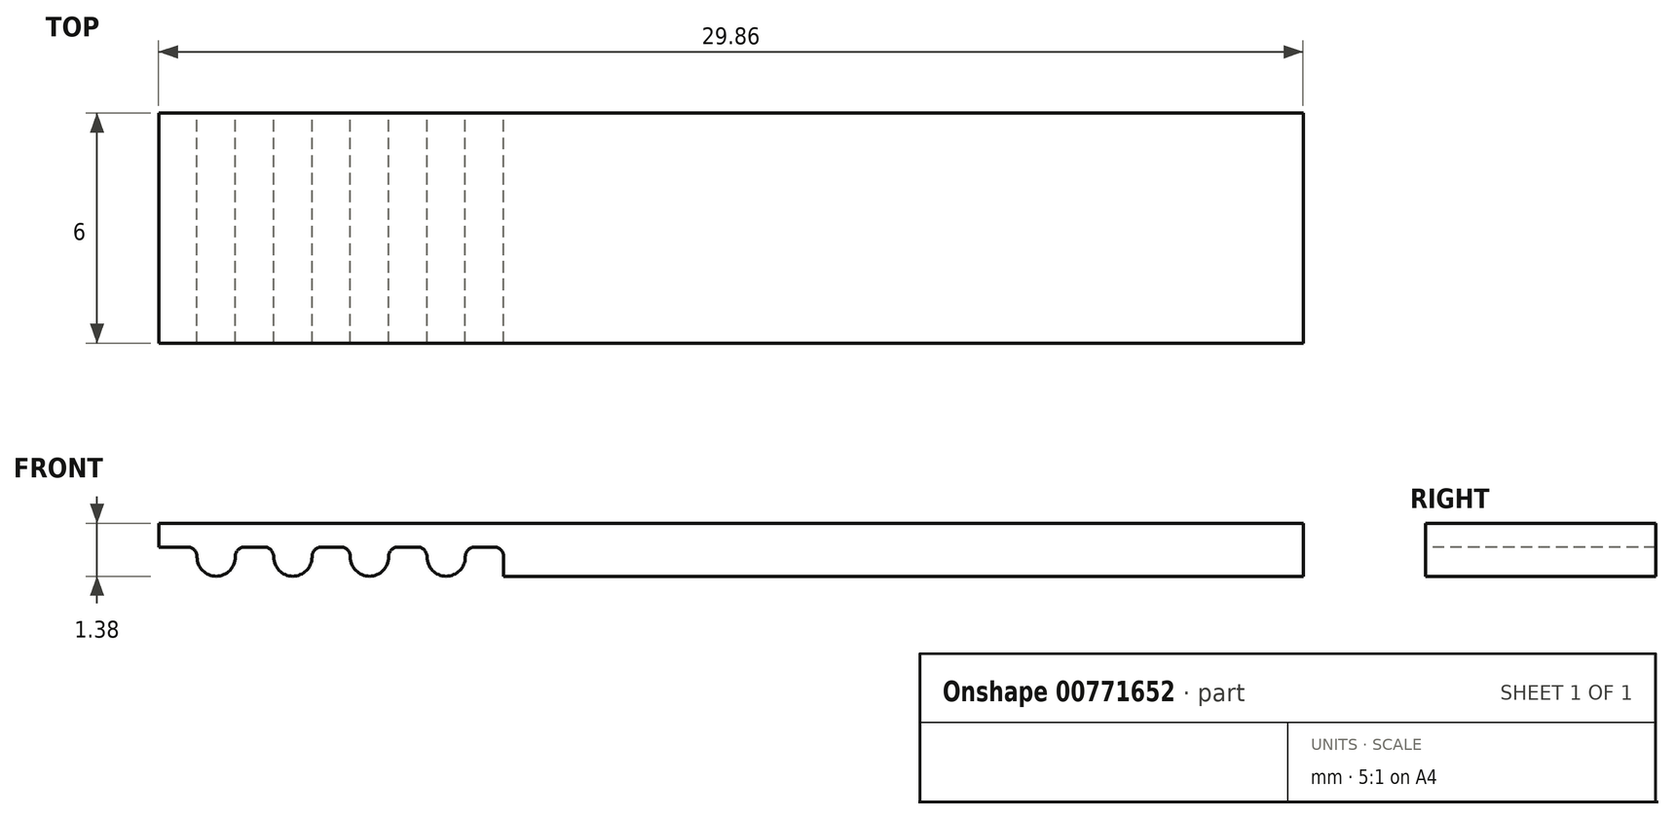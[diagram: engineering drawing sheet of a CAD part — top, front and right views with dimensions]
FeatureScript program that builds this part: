
annotation { "Feature Type Name" : "Feature", "Feature Type Description" : "" }
export const myFeature = defineFeature(function(context is Context, id is Id, definition is map)
    precondition{}
    {
        {
            var Q0;
            Q0=qCreatedBy(makeId("Top.planeOp"),FACE);
            var sketch = newSketch(context, id + "F0", { "sketchPlane" : qUnion([Q0])});
            skLineSegment(sketch, "E0.bottom", {"start": v(-11.94, 3) * mm, "end": v(17.92, 3) * mm});
            skLineSegment(sketch, "E0.top", {"start": v(-11.94, -3) * mm, "end": v(17.92, -3) * mm});
            skLineSegment(sketch, "E0.left", {"start": v(-11.94, 3) * mm, "end": v(-11.94, -3) * mm});
            skLineSegment(sketch, "E0.right", {"start": v(17.92, 3) * mm, "end": v(17.92, -3) * mm});
            skSolve(sketch);
        }
        {
            var Q0;
            Q0 = qSketchRegion(id + "F0", true);
            extrude(context, id + "F1", {"entities" : qUnion([Q0]), "depth" : 1.38 * mm, "offsetDistance" : 25 * mm});
        }
        {
            var Q0;
            Q0=makeQuery(id+"F1.opExtrude","CAP_FACE",FACE,{"disambiguationData":[OSD([sQuery(id+"F0.wireOp",EDGE,"E0.bottom"),sQuery(id+"F0.wireOp",EDGE,"E0.top"),sQuery(id+"F0.wireOp",EDGE,"E0.left"),sQuery(id+"F0.wireOp",EDGE,"E0.right")])],"isStart":true});
            var sketch = newSketch(context, id + "F2", { "sketchPlane" : qUnion([Q0])});
            skLineSegment(sketch, "E1.bottom", {"start": v(-11.94, 3) * mm, "end": v(-10.94, 3) * mm});
            skLineSegment(sketch, "E1.top", {"start": v(-11.94, -3) * mm, "end": v(-10.94, -3) * mm});
            skLineSegment(sketch, "E1.left", {"start": v(-11.94, 3) * mm, "end": v(-11.94, -3) * mm});
            skLineSegment(sketch, "E1.right", {"start": v(-10.94, 3) * mm, "end": v(-10.94, -3) * mm});
            skLineSegment(sketch, "E2.bottom", {"start": v(-9.94, 3) * mm, "end": v(-8.94, 3) * mm});
            skLineSegment(sketch, "E2.top", {"start": v(-9.94, -3) * mm, "end": v(-8.94, -3) * mm});
            skLineSegment(sketch, "E2.left", {"start": v(-9.94, 3) * mm, "end": v(-9.94, -3) * mm});
            skLineSegment(sketch, "E2.right", {"start": v(-8.94, 3) * mm, "end": v(-8.94, -3) * mm});
            skLineSegment(sketch, "E3.bottom", {"start": v(-7.94, 3) * mm, "end": v(-6.94, 3) * mm});
            skLineSegment(sketch, "E3.top", {"start": v(-7.94, -3) * mm, "end": v(-6.94, -3) * mm});
            skLineSegment(sketch, "E3.left", {"start": v(-7.94, 3) * mm, "end": v(-7.94, -3) * mm});
            skLineSegment(sketch, "E3.right", {"start": v(-6.94, 3) * mm, "end": v(-6.94, -3) * mm});
            skLineSegment(sketch, "E4.bottom", {"start": v(-5.94, 3) * mm, "end": v(-4.94, 3) * mm});
            skLineSegment(sketch, "E4.top", {"start": v(-5.94, -3) * mm, "end": v(-4.94, -3) * mm});
            skLineSegment(sketch, "E4.left", {"start": v(-5.94, 3) * mm, "end": v(-5.94, -3) * mm});
            skLineSegment(sketch, "E4.right", {"start": v(-4.94, 3) * mm, "end": v(-4.94, -3) * mm});
            skLineSegment(sketch, "E5.bottom", {"start": v(-3.94, 3) * mm, "end": v(-2.94, 3) * mm});
            skLineSegment(sketch, "E5.top", {"start": v(-3.94, -3) * mm, "end": v(-2.94, -3) * mm});
            skLineSegment(sketch, "E5.left", {"start": v(-3.94, 3) * mm, "end": v(-3.94, -3) * mm});
            skLineSegment(sketch, "E5.right", {"start": v(-2.94, 3) * mm, "end": v(-2.94, -3) * mm});
            skSolve(sketch);
        }
        {
            var Q0;
            Q0 = qSketchRegion(id + "F2", true);
            extrude(context, id + "F3", {"entities" : qUnion([Q0]), "operationType" : NewBodyOperationType.REMOVE, "oppositeDirection" : true, "depth" : 0.76 * mm, "offsetDistance" : 25 * mm});
        }
        {
            var Q0;
            Q0=makeQuery(id+"F3.boolean.opBoolean","COPY",EDGE,{"derivedFrom":makeQuery(id+"F3.opExtrude","CAP_EDGE",EDGE,{"disambiguationData":[OSD([sQuery(id+"F2.wireOp",EDGE,"E1.right")])],"isStart":true})});
            var Q1;
            Q1=makeQuery(id+"F3.boolean.opBoolean","COPY",EDGE,{"derivedFrom":makeQuery(id+"F3.opExtrude","CAP_EDGE",EDGE,{"disambiguationData":[OSD([sQuery(id+"F2.wireOp",EDGE,"E2.left")])],"isStart":true})});
            var Q2;
            Q2=makeQuery(id+"F3.boolean.opBoolean","COPY",EDGE,{"derivedFrom":makeQuery(id+"F3.opExtrude","CAP_EDGE",EDGE,{"disambiguationData":[OSD([sQuery(id+"F2.wireOp",EDGE,"E2.right")])],"isStart":true})});
            var Q3;
            Q3=makeQuery(id+"F3.boolean.opBoolean","COPY",EDGE,{"derivedFrom":makeQuery(id+"F3.opExtrude","CAP_EDGE",EDGE,{"disambiguationData":[OSD([sQuery(id+"F2.wireOp",EDGE,"E3.left")])],"isStart":true})});
            var Q4;
            Q4=makeQuery(id+"F3.boolean.opBoolean","COPY",EDGE,{"derivedFrom":makeQuery(id+"F3.opExtrude","CAP_EDGE",EDGE,{"disambiguationData":[OSD([sQuery(id+"F2.wireOp",EDGE,"E3.right")])],"isStart":true})});
            var Q5;
            Q5=makeQuery(id+"F3.boolean.opBoolean","COPY",EDGE,{"derivedFrom":makeQuery(id+"F3.opExtrude","CAP_EDGE",EDGE,{"disambiguationData":[OSD([sQuery(id+"F2.wireOp",EDGE,"E4.left")])],"isStart":true})});
            var Q6;
            Q6=makeQuery(id+"F3.boolean.opBoolean","COPY",EDGE,{"derivedFrom":makeQuery(id+"F3.opExtrude","CAP_EDGE",EDGE,{"disambiguationData":[OSD([sQuery(id+"F2.wireOp",EDGE,"E4.right")])],"isStart":true})});
            var Q7;
            Q7=makeQuery(id+"F3.boolean.opBoolean","COPY",EDGE,{"derivedFrom":makeQuery(id+"F3.opExtrude","CAP_EDGE",EDGE,{"disambiguationData":[OSD([sQuery(id+"F2.wireOp",EDGE,"E5.left")])],"isStart":true})});
            fillet(context, id + "F4", {"entities" : qUnion([Q0, Q1, Q2, Q3, Q4, Q5, Q6, Q7]), "radius" : 0.5 * mm, "tangentPropagation" : true, "allowEdgeOverflow" : false});
        }
        {
            var Q0;
            Q0=makeQuery(id+"F3.boolean.opBoolean","COPY",EDGE,{"derivedFrom":makeQuery(id+"F3.opExtrude","CAP_EDGE",EDGE,{"disambiguationData":[OSD([sQuery(id+"F2.wireOp",EDGE,"E1.right")])],"isStart":false})});
            var Q1;
            Q1=makeQuery(id+"F3.boolean.opBoolean","COPY",EDGE,{"derivedFrom":makeQuery(id+"F3.opExtrude","CAP_EDGE",EDGE,{"disambiguationData":[OSD([sQuery(id+"F2.wireOp",EDGE,"E2.left")])],"isStart":false})});
            var Q2;
            Q2=makeQuery(id+"F3.boolean.opBoolean","COPY",EDGE,{"derivedFrom":makeQuery(id+"F3.opExtrude","CAP_EDGE",EDGE,{"disambiguationData":[OSD([sQuery(id+"F2.wireOp",EDGE,"E2.right")])],"isStart":false})});
            var Q3;
            Q3=makeQuery(id+"F3.boolean.opBoolean","COPY",EDGE,{"derivedFrom":makeQuery(id+"F3.opExtrude","CAP_EDGE",EDGE,{"disambiguationData":[OSD([sQuery(id+"F2.wireOp",EDGE,"E3.right")])],"isStart":false})});
            var Q4;
            Q4=makeQuery(id+"F3.boolean.opBoolean","COPY",EDGE,{"derivedFrom":makeQuery(id+"F3.opExtrude","CAP_EDGE",EDGE,{"disambiguationData":[OSD([sQuery(id+"F2.wireOp",EDGE,"E4.right")])],"isStart":false})});
            var Q5;
            Q5=makeQuery(id+"F3.boolean.opBoolean","COPY",EDGE,{"derivedFrom":makeQuery(id+"F3.opExtrude","CAP_EDGE",EDGE,{"disambiguationData":[OSD([sQuery(id+"F2.wireOp",EDGE,"E5.right")])],"isStart":false})});
            var Q6;
            Q6=makeQuery(id+"F3.boolean.opBoolean","COPY",EDGE,{"derivedFrom":makeQuery(id+"F3.opExtrude","CAP_EDGE",EDGE,{"disambiguationData":[OSD([sQuery(id+"F2.wireOp",EDGE,"E5.left")])],"isStart":false})});
            var Q7;
            Q7=makeQuery(id+"F3.boolean.opBoolean","COPY",EDGE,{"derivedFrom":makeQuery(id+"F3.opExtrude","CAP_EDGE",EDGE,{"disambiguationData":[OSD([sQuery(id+"F2.wireOp",EDGE,"E4.left")])],"isStart":false})});
            var Q8;
            Q8=makeQuery(id+"F3.boolean.opBoolean","COPY",EDGE,{"derivedFrom":makeQuery(id+"F3.opExtrude","CAP_EDGE",EDGE,{"disambiguationData":[OSD([sQuery(id+"F2.wireOp",EDGE,"E3.left")])],"isStart":false})});
            fillet(context, id + "F5", {"entities" : qUnion([Q0, Q1, Q2, Q3, Q4, Q5, Q6, Q7, Q8]), "radius" : 0.25 * mm, "tangentPropagation" : true, "allowEdgeOverflow" : false});
        }
    });
